# Revit family: Equal_Double_Bowl_Drop-in_ADA_Sink-Elkay-LRAD3322601_4_MR2
name_source: partatom
category: Plumbing Fixtures
units: mm (PartAtom-declared; Revit-internal decimal feet)

## family parameters
Cut with Voids When Loaded = No
Host = Face
Maintain Annotation Orientation = No
OmniClass Number = 23.45.05.14.14
OmniClass Title = Sinks/Lavatories
Part Type = Normal
Room Calculation Point = No
Round Connector Dimension = Use Diameter
Shared = No

## types (5) — shared parameters
Approx. Shipping Weight (lbs) = 23
Assembly Code = D2010410
Back Flange = 4.125 "
Bowl 1 Dimensions = 13 1/2 inch x 16 inch x 5 5/8 inch
Bowl 2 Dimensions = 13 1/2 inch x 16 inch x 5 5/8 inch
Bowl Depth = 5.625 "
Bowl Length 2 = 13.5 "
Bowl Length1 = 13.5 "
Bowl Width = 16 "
CL of Faucet Hole = 1.75 "
Cutting Length = 32.375 "
Cutting Width = 21.375 "
Darin and Pitch height = 0.65 "
Default Elevation = 48 "
Description = Lustertone® Classic Stainless Steel 33 inch x 22 inch x 6 inch Equal Double Bowl Drop-in ADA Sink
Distance B/W 2 Bowls = 1.25 "
Drain Location = Rear Center
Drain Location Along X- Axis = 6.75 "
Drain Location Along Y- Axis = 5 "
Drain Size = 3.5 "
Front Flange = 1.875 "
Gauge = 18
Hole-2 = Yes
Hole-5 = No
Installation Type = Drop-in
Left Flange = 2.375 "
Length of Sink = 33 "
Main Material = Finish-Elkay-Stainless Steel
Manufacturer = Elkay Manufacturer Company
Manufacturer Brand = Elkay (by Zurn Elkay Water Solutions)
Masking Region for Bowl = 1.75 "
Number of Bowls = 2
Outlet Connection Size (inch) = 1.5 "
Product Documentation Link = https://www.elkayfiles.com
Product Installation Sheet URL = https://www.elkayfiles.com
Product Page URL = https://www.elkay.com
Product Weight (lbs) = 21
R1 for Rim = 0.09 "
R2 for Rim = 0.06 "
Radius for Bowl = 1.76 "
Radius for cutting edge = 1.5 "
Repair Parts URL = https://www.elkayfiles.com
Right Flange = 2.375 "
Rim Height = 0.375 "
Sink Depth = 6 "
Sink Dimensions = 33 inch x 22 inch x 6 inch
U-channel Length along -X axis = 28 "
U-channel Length along -Y axis = 17 "
URL = https://www.elkay.com
Vertical Radius = 1.75 "
Waste Connection = No
Width of Sink = 22 "
zero-valued in all types: OS4

## per-type parameters (varying)
| type | HW Connection | Hole 2 | Hole-1 | Hole-3 | Hole-4 | ML2 | MR2 | Model | No of Hole configurations |
| LRAD3322601(Double Bowl Drop-in ADA Sink) | No | 16.5 " | No | No | No | 0 | 0 | LRAD3322601 | 1 |
| LRAD3322602(Double Bowl Drop-in ADA Sink) | Yes | 14.5 " | No | Yes | No | 0 | 1 | LRAD3322602 | 2 |
| LRAD3322603(Double Bowl Drop-in ADA Sink) | No | 16.5 " | Yes | Yes | No | 1 | 1 | LRAD3322603 | 3 |
| LRAD3322604(Double Bowl Drop-in ADA Sink) | No | 16.5 " | Yes | Yes | Yes | 1 | 1 | LRAD3322604 | 4 |
| LRAD332260MR2(Double Bowl Drop-in ADA Sink) | No | 16.5 " | No | Yes | No | 0 | 1 | LRAD332260MR2 | 1 |

## geometry (parser evidence)
native form markers: Sweep x5
no freeform markers — native parametric forms only
